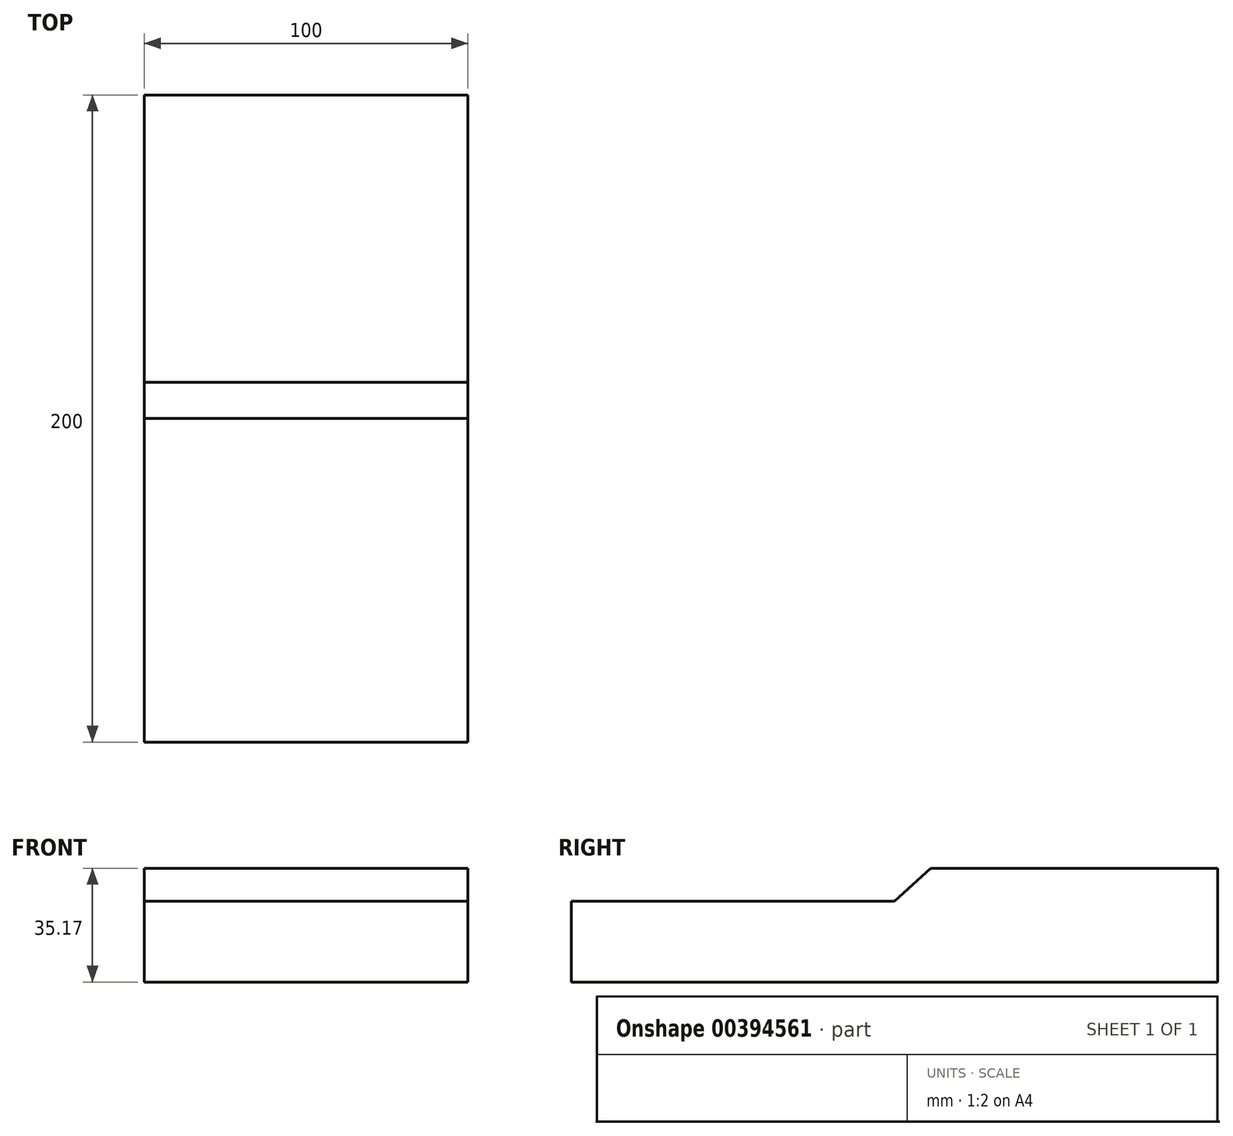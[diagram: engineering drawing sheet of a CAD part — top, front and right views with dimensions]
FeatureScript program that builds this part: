
annotation { "Feature Type Name" : "Feature", "Feature Type Description" : "" }
export const myFeature = defineFeature(function(context is Context, id is Id, definition is map)
    precondition{}
    {
        {
            var Q0;
            Q0=qCreatedBy(makeId("Top.planeOp"),FACE);
            var sketch = newSketch(context, id + "F0", { "sketchPlane" : qUnion([Q0])});
            skLineSegment(sketch, "E0.bottom", {"start": v(50, -100) * mm, "end": v(-50, -100) * mm});
            skLineSegment(sketch, "E0.top", {"start": v(50, 100) * mm, "end": v(-50, 100) * mm});
            skLineSegment(sketch, "E0.left", {"start": v(50, -100) * mm, "end": v(50, 100) * mm});
            skLineSegment(sketch, "E0.right", {"start": v(-50, -100) * mm, "end": v(-50, 100) * mm});
            skPoint(sketch, "E0.middle", {"position": v(0, 0) * mm});
            skSolve(sketch);
        }
        {
            var Q0;
            Q0=makeQuery(id+"F0.imprint","IMPRINT",FACE,{"disambiguationData":[TD([[makeQuery(id+"F0.imprint","IMPRINT",EDGE,{"derivedFrom":sQuery(id+"F0.wireOp",EDGE,"E0.bottom")}),-1.0]])]});
            extrude(context, id + "F1", {"entities" : qUnion([Q0]), "depth" : 25 * mm});
        }
        {
            var Q0;
            Q0=makeQuery(id+"F1.opExtrude","SWEPT_FACE",FACE,{"disambiguationData":[OSD([sQuery(id+"F0.wireOp",EDGE,"E0.left")])]});
            var sketch = newSketch(context, id + "F2", { "sketchPlane" : qUnion([Q0])});
            skLineSegment(sketch, "E1.bottom", {"start": v(100, 25) * mm, "end": v(0, 25) * mm});
            skLineSegment(sketch, "E1.top", {"start": v(100, 35.17) * mm, "end": v(0, 35.17) * mm});
            skLineSegment(sketch, "E1.left", {"start": v(100, 25) * mm, "end": v(100, 35.17) * mm});
            skLineSegment(sketch, "E1.right", {"start": v(0, 25) * mm, "end": v(0, 35.17) * mm});
            skSolve(sketch);
        }
        {
            var Q0;
            Q0=makeQuery(id+"F2.imprint","IMPRINT",FACE,{"disambiguationData":[TD([[makeQuery(id+"F2.imprint","IMPRINT",EDGE,{"derivedFrom":sQuery(id+"F2.wireOp",EDGE,"E1.bottom")}),1.0]])]});
            extrude(context, id + "F3", {"entities" : qUnion([Q0]), "operationType" : NewBodyOperationType.ADD, "oppositeDirection" : true, "depth" : 100 * mm});
        }
        {
            var Q0;
            Q0=makeQuery(id+"F3.boolean.opBoolean","MERGE",FACE,{"derivedFrom":[makeQuery(id+"F1.opExtrude","SWEPT_FACE",FACE,{"disambiguationData":[OSD([sQuery(id+"F0.wireOp",EDGE,"E0.left")])]}),makeQuery(id+"F3.opExtrude","CAP_FACE",FACE,{"disambiguationData":[OSD([sQuery(id+"F2.wireOp",EDGE,"E1.bottom"),sQuery(id+"F2.wireOp",EDGE,"E1.top"),sQuery(id+"F2.wireOp",EDGE,"E1.left"),sQuery(id+"F2.wireOp",EDGE,"E1.right")])],"isStart":true})]});
            var sketch = newSketch(context, id + "F4", { "sketchPlane" : qUnion([Q0])});
            skLineSegment(sketch, "E2", {"start": v(20.27, 25.17) * mm, "end": v(100, 25) * mm, "construction": true});
            skLineSegment(sketch, "E3", {"start": v(0, 25) * mm, "end": v(11.17, 35.17) * mm});
            skLineSegment(sketch, "E4", {"start": v(11.17, 35.17) * mm, "end": v(20.27, 25.17) * mm, "construction": true});
            skLineSegment(sketch, "E5", {"start": v(20.27, 25.17) * mm, "end": v(31.25, 35.17) * mm});
            skSolve(sketch);
        }
        {
            var Q0;
            {var subQ0=sQuery(id+"F4.wireOp",EDGE,"E3");Q0=makeQuery(id+"F4.imprint","IMPRINT",FACE,{"disambiguationData":[TD([[makeQuery(id+"F4.imprint","IMPRINT",EDGE,{"derivedFrom":subQ0}),1.0]])]});}
            extrude(context, id + "F5", {"entities" : qUnion([Q0]), "operationType" : NewBodyOperationType.REMOVE, "oppositeDirection" : true, "depth" : 200 * mm});
        }
    });
